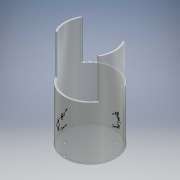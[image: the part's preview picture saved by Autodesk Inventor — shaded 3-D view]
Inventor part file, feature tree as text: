
AUTODESK INVENTOR PART (.ipt)
format: ipt  version: 2016 (Build 200138000, 138)  size: 224,256 bytes
history: native  units: mm
features: sketch x14, other x6, extrude x5, hole x4
ambient origin geometry x8: Origin, YZ Plane, XZ Plane, XY Plane, X Axis, Y Axis, Z Axis, Center Point
bodies: Body1 (feature_tree)
feature tree (29):
  other  "ソリッド1"
  extrude  "押し出し1"  Depth=102.0mm
  sketch  "スケッチ2"
  other  "作業平面1"
  other  "作業平面2"
  other  "作業平面3"
  other  "作業平面4"
  sketch  "スケッチ3"
  sketch  "スケッチ4"
  sketch  "スケッチ5"
  sketch  "スケッチ6"
  other  "作業平面5"
  extrude  "押し出し9"  Depth=110.0mm
  sketch  "スケッチ9"
  extrude  "押し出し12"  TaperAngle=30.0deg  [1 undecoded]
  extrude  "押し出し13"  TaperAngle=150.0deg  [1 undecoded]
  sketch  "スケッチ12"
  sketch  "スケッチ13"
  sketch  "スケッチ14"
  sketch  "スケッチ15"
  extrude  "押し出し18"  Depth=20.0mm TaperAngle=0.0deg
  hole  "穴9"  [1 undecoded]
  hole  "穴10"  [1 undecoded]
  hole  "穴11"  [1 undecoded]
  hole  "穴12"  [1 undecoded]
  sketch  "スケッチ1"
  sketch  "スケッチ10"
  sketch  "スケッチ11"
  sketch  "スケッチ16"
note: 6 required parameter values undecoded (feature->parameter linkage not recoverable at this tier; creation-order binding heuristic only, values carry confidence <= 0.55)
